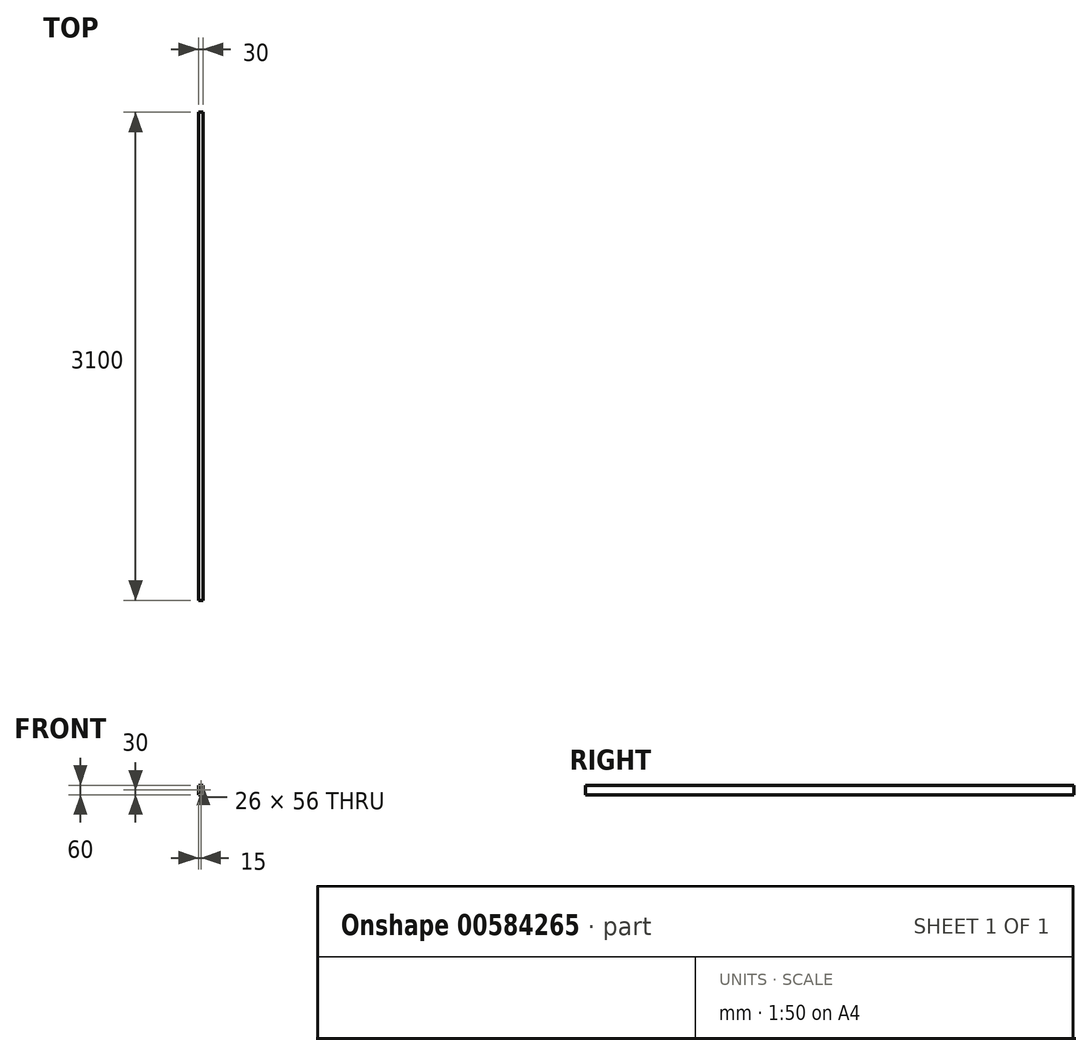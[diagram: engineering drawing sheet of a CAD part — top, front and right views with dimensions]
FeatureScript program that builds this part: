
annotation { "Feature Type Name" : "Feature", "Feature Type Description" : "" }
export const myFeature = defineFeature(function(context is Context, id is Id, definition is map)
    precondition{}
    {
        {
            var Q0;
            Q0=qCreatedBy(makeId("Front.planeOp"),FACE);
            var sketch = newSketch(context, id + "F0", { "sketchPlane" : qUnion([Q0])});
            skLineSegment(sketch, "E0.bottom", {"start": v(0, 0) * mm, "end": v(30, 0) * mm});
            skLineSegment(sketch, "E0.top", {"start": v(0, 60) * mm, "end": v(30, 60) * mm});
            skLineSegment(sketch, "E0.left", {"start": v(0, 0) * mm, "end": v(0, 60) * mm});
            skLineSegment(sketch, "E0.right", {"start": v(30, 0) * mm, "end": v(30, 60) * mm});
            skLineSegment(sketch, "E1.bottom", {"start": v(2, 58) * mm, "end": v(28, 58) * mm});
            skLineSegment(sketch, "E1.top", {"start": v(2, 2) * mm, "end": v(28, 2) * mm});
            skLineSegment(sketch, "E1.left", {"start": v(2, 58) * mm, "end": v(2, 2) * mm});
            skLineSegment(sketch, "E1.right", {"start": v(28, 58) * mm, "end": v(28, 2) * mm});
            skSolve(sketch);
        }
        {
            var Q0;
            Q0=makeQuery(id+"F0.imprint","IMPRINT",FACE,{"disambiguationData":[TD([[makeQuery(id+"F0.imprint","IMPRINT",EDGE,{"derivedFrom":sQuery(id+"F0.wireOp",EDGE,"E0.bottom")}),1.0]])]});
            extrude(context, id + "F1", {"entities" : qUnion([Q0]), "depth" : 3100 * mm, "offsetDistance" : 25 * mm});
        }
    });
